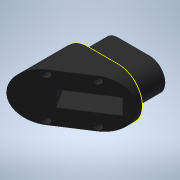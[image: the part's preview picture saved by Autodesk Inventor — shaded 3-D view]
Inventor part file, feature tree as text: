
AUTODESK INVENTOR PART (.ipt)
format: ipt  version: 2020 (Build 240168000, 168)  size: 305,152 bytes
history: native  units: mm
features: reference x9, sketch x6, extrude x6, other x5, projected_geometry x3, split x1, fillet x1, plane x1, hole x1
ambient origin geometry x8: Origin, YZ Plane, XZ Plane, XY Plane, X Axis, Y Axis, Z Axis, Center Point
bodies: Solid1 (feature_tree), Solid2 (feature_tree), Solid3 (feature_tree)
feature tree (33):
  sketch  "Sketch1"  dims[d0=30.0mm d1=0.0mm d2=70.0mm d3=0.0mm]
  extrude  "Extrusion1"  Depth=30.0mm TaperAngle=0.0deg
  extrude  "Extrusion2"  Depth=46.0mm
  extrude  "Extrusion3"  Depth=35.0mm TaperAngle=0.0deg
  extrude  "Extrusion4"  Depth=0.5mm
  extrude  "Extrusion5"  Depth=0.5mm
  extrude  "Extrusion6"  Depth=8.0mm
  split  "Split1"
  fillet  "Fillet1"  Radius=0.5mm
  plane  "Work Plane1"
  hole  "Hole1"  [1 undecoded]
  reference  "Reference1"
  sketch  "Sketch2"  dims[d4=100.0mm d5=0.0mm d6=46.0mm]
  reference  "Reference2"
  sketch  "Sketch3"  dims[d7=15.0mm d8=35.0mm d9=0.0mm]
  reference  "Reference3"
  reference  "Reference4"
  sketch  "Sketch5"  dims[d10=0.1mm d11=0.5mm]
  reference  "Reference10"
  reference  "Reference11"
  reference  "Reference12"
  reference  "Reference13"
  reference  "Reference14"
  sketch  "Sketch6"  dims[d12=0.5mm d13=0.5mm]
  projected_geometry  "Projected Loop1"
  sketch  "Sketch7"  dims[d14=0.5mm d15=0.5mm d16=0.5mm d17=20.1mm d18=0.0mm d19=6.0mm d20=40.0mm d21=0.0mm d22=8.0mm d23=-85.0mm d24=3.0mm d25=6.0mm d26=6.0mm d27=50.0mm d28=90.0deg d29=8.0mm d30=20.594885mm]
  projected_geometry  "Projected Loop2"
  projected_geometry  "Projected Loop3"
  other  "<userpath>\Documents\GitHub\OpenRaman\Hardware\OpenRaman.V1.iam"
  other  "OpenRaman.V1.iam"
  other  "SpectometerTube:1"
  other  "TCD1304AP:1"
  other  "PrismsGeometry:1"
note: 1 required parameter value undecoded (feature->parameter linkage not recoverable at this tier; creation-order binding heuristic only, values carry confidence <= 0.55)
